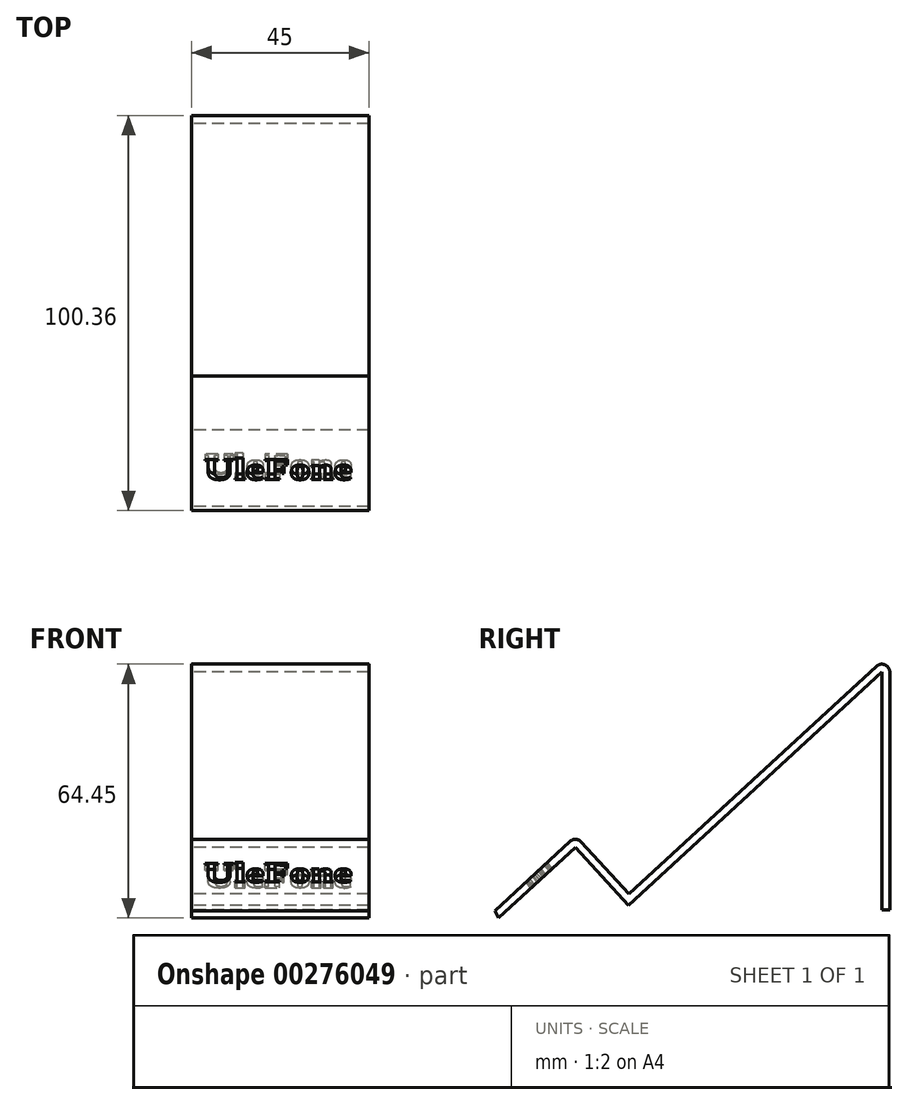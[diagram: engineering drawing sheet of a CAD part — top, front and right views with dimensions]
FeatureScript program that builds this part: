
annotation { "Feature Type Name" : "Feature", "Feature Type Description" : "" }
export const myFeature = defineFeature(function(context is Context, id is Id, definition is map)
    precondition{}
    {
        {
            var Q0;
            Q0=qCreatedBy(makeId("Right.planeOp"),FACE);
            var sketch = newSketch(context, id + "F0", { "sketchPlane" : qUnion([Q0])});
            skLineSegment(sketch, "E0", {"start": v(0, 0) * mm, "end": v(66.2, 60.96) * mm});
            skLineSegment(sketch, "E1", {"start": v(66.2, 60.96) * mm, "end": v(66.2, -4.04) * mm});
            skLineSegment(sketch, "E2", {"start": v(0, 0) * mm, "end": v(-13.55, 14.71) * mm});
            skLineSegment(sketch, "E3", {"start": v(-13.55, 14.71) * mm, "end": v(-34.15, -4.25) * mm});
            skLineSegment(sketch, "E4.0", {"start": v(64.2, 56.4) * mm, "end": v(64.2, -4.04) * mm});
            skLineSegment(sketch, "E4.1", {"start": v(-0.12, -2.83) * mm, "end": v(64.2, 56.4) * mm});
            skLineSegment(sketch, "E4.2", {"start": v(-0.12, -2.83) * mm, "end": v(-13.66, 11.89) * mm});
            skLineSegment(sketch, "E4.3", {"start": v(-13.66, 11.89) * mm, "end": v(-33.15, -6.05) * mm});
            skLineSegment(sketch, "E5", {"start": v(-33.15, -6.05) * mm, "end": v(-34.15, -4.25) * mm});
            skLineSegment(sketch, "E6", {"start": v(66.2, -4.04) * mm, "end": v(64.2, -4.04) * mm});
            skSolve(sketch);
        }
        {
            var Q0;
            Q0 = qSketchRegion(id + "F0", true);
            extrude(context, id + "F1", {"entities" : qUnion([Q0]), "depth" : 45 * mm});
        }
        {
            var Q0;
            Q0=makeQuery(id+"F1.opExtrude","SWEPT_EDGE",EDGE,{"disambiguationData":[OSD([sQuery(id+"F0.wireOp",EDGE,"E0"),sQuery(id+"F0.wireOp",EDGE,"E1")])]});
            var Q1;
            Q1=makeQuery(id+"F1.opExtrude","SWEPT_EDGE",EDGE,{"disambiguationData":[OSD([sQuery(id+"F0.wireOp",EDGE,"E2"),sQuery(id+"F0.wireOp",EDGE,"E3")])]});
            fillet(context, id + "F2", {"entities" : qUnion([Q0, Q1]), "radius" : 2 * mm, "tangentPropagation" : true, "allowEdgeOverflow" : false});
        }
        {
            var Q0;
            Q0=makeQuery(id+"F1.opExtrude","SWEPT_FACE",FACE,{"disambiguationData":[OSD([sQuery(id+"F0.wireOp",EDGE,"E3")])]});
            var sketch = newSketch(context, id + "F3", { "sketchPlane" : qUnion([Q0])});
            skText(sketch, "E7", { "text": "UleFone", "fontName": "Tinos-Bold.ttf"});
            const initialGuessF3  = {"E7": [0.00315, -0.01724, 1, 0, 0.00762]};
            skSetInitialGuess(sketch, initialGuessF3);
            skSolve(sketch);
        }
        {
            var Q0;
            Q0 = qSketchRegion(id + "F3", true);
            extrude(context, id + "F4", {"entities" : qUnion([Q0]), "operationType" : NewBodyOperationType.REMOVE, "oppositeDirection" : true, "depth" : 25 * mm});
        }
    });
